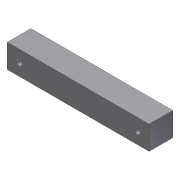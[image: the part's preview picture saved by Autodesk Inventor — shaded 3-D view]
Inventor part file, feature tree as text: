
AUTODESK INVENTOR PART (.ipt)
format: ipt  version: 2012 (Build 160160000, 160)  size: 75,264 bytes
history: native  units: in
note: dims shown in document units (in); Inventor stores cm internally (conversion verified against a paired STEP export)
features: extrude x1, sketch x1
ambient origin geometry x8: Origin, YZ Plane, XZ Plane, XY Plane, X Axis, Y Axis, Z Axis, Center Point
bodies: Solid1 (feature_tree)
feature tree (2):
  extrude  "Extrusion1"  Depth=6.0in
  sketch  "Sketch1"  dims[d0=1.0in d1=6.0in d2=0.25in d3=0.25in d4=0.5in d5=0.5in d6=0.5in d7=0.5in d8=1.0in d9=0.0in]
